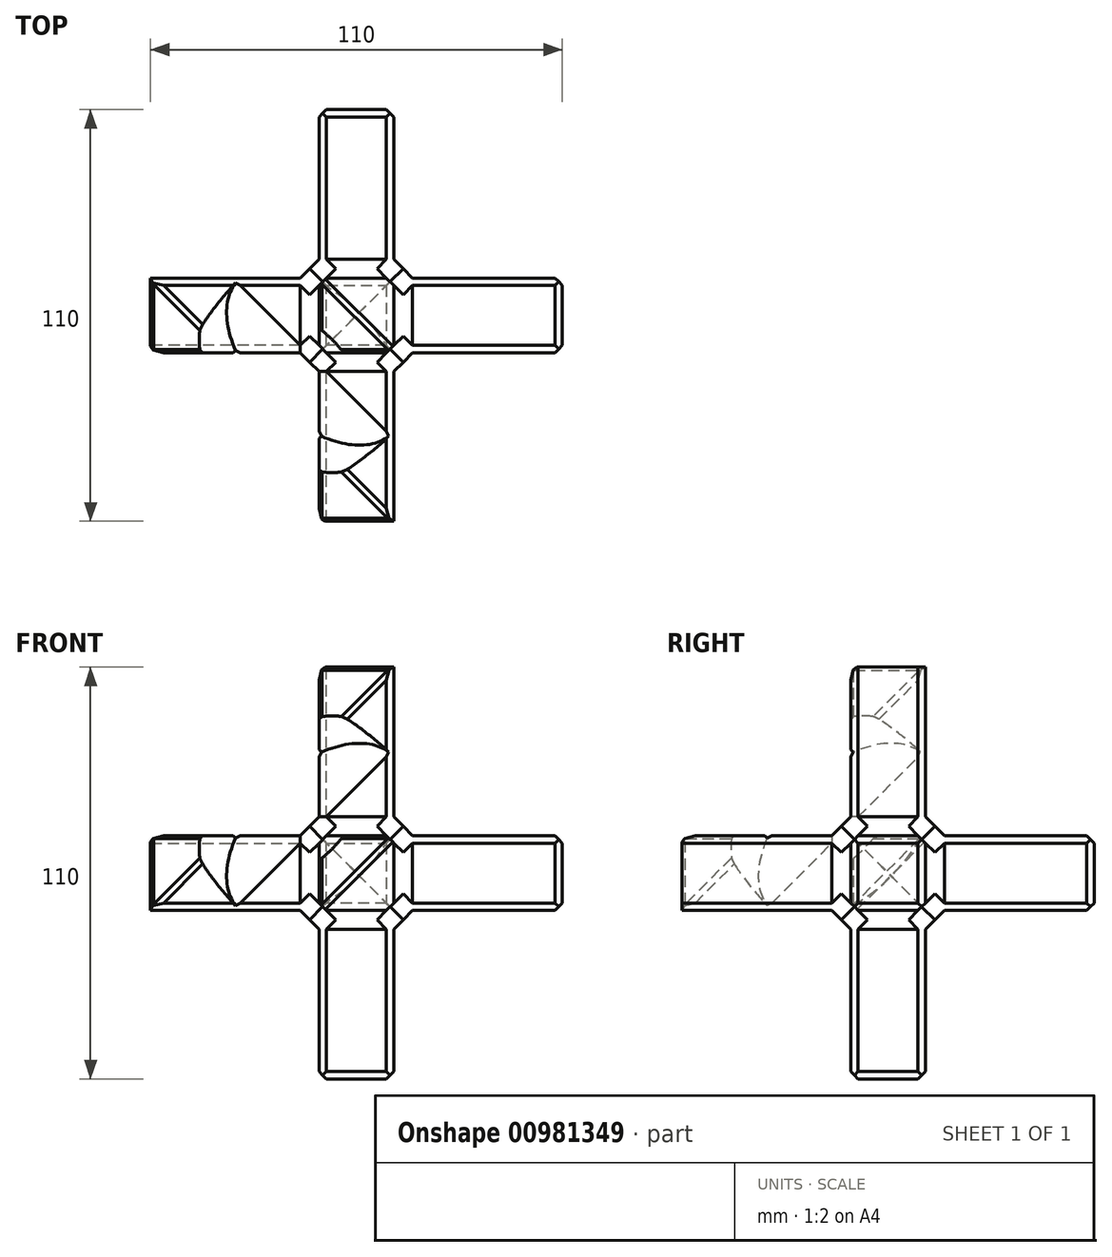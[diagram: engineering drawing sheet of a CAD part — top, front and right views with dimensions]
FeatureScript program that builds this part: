
annotation { "Feature Type Name" : "Feature", "Feature Type Description" : "" }
export const myFeature = defineFeature(function(context is Context, id is Id, definition is map)
    precondition{}
    {
        {
            assignVariable(context, id + "F0", {"name" : "longueur", "anyValue" : 110});
        }
        {
            assignVariable(context, id + "F1", {"name" : "HautBougie", "anyValue" : 23});
        }
        {
            var Q0;
            Q0=qCreatedBy(makeId("Top.planeOp"),FACE);
            var sketch = newSketch(context, id + "F2", { "sketchPlane" : qUnion([Q0])});
            skLineSegment(sketch, "E0.bottom", {"start": v(10, 10) * mm, "end": v(-10, 10) * mm});
            skLineSegment(sketch, "E0.top", {"start": v(10, -10) * mm, "end": v(-10, -10) * mm});
            skLineSegment(sketch, "E0.left", {"start": v(10, 10) * mm, "end": v(10, -10) * mm});
            skLineSegment(sketch, "E0.right", {"start": v(-10, 10) * mm, "end": v(-10, -10) * mm});
            skPoint(sketch, "E0.middle", {"position": v(0, 0) * mm});
            skSolve(sketch);
        }
        {
            var Q0;
            Q0 = qSketchRegion(id + "F2", true);
            extrude(context, id + "F3", {"entities" : qUnion([Q0]), "endBound" : BoundingType.SYMMETRIC, "depth" : (getVariable(context, 'longueur')) * mm, "offsetDistance" : 25 * mm});
        }
        {
            var Q0;
            Q0=qCreatedBy(makeId("Right.planeOp"),FACE);
            var sketch = newSketch(context, id + "F4", { "sketchPlane" : qUnion([Q0])});
            skLineSegment(sketch, "E1.bottom", {"start": v(-10, 10) * mm, "end": v(10, 10) * mm});
            skLineSegment(sketch, "E1.top", {"start": v(-10, -10) * mm, "end": v(10, -10) * mm});
            skLineSegment(sketch, "E1.left", {"start": v(-10, 10) * mm, "end": v(-10, -10) * mm});
            skLineSegment(sketch, "E1.right", {"start": v(10, 10) * mm, "end": v(10, -10) * mm});
            skPoint(sketch, "E1.middle", {"position": v(0, 0) * mm});
            skSolve(sketch);
        }
        {
            var Q0;
            Q0 = qSketchRegion(id + "F4", true);
            extrude(context, id + "F5", {"entities" : qUnion([Q0]), "operationType" : NewBodyOperationType.ADD, "endBound" : BoundingType.SYMMETRIC, "depth" : (getVariable(context, 'longueur')) * mm, "offsetDistance" : 25 * mm});
        }
        {
            var Q0;
            Q0=qCreatedBy(makeId("Front.planeOp"),FACE);
            var sketch = newSketch(context, id + "F6", { "sketchPlane" : qUnion([Q0])});
            skLineSegment(sketch, "E2.bottom", {"start": v(10, 10) * mm, "end": v(-10, 10) * mm});
            skLineSegment(sketch, "E2.top", {"start": v(10, -10) * mm, "end": v(-10, -10) * mm});
            skLineSegment(sketch, "E2.left", {"start": v(10, 10) * mm, "end": v(10, -10) * mm});
            skLineSegment(sketch, "E2.right", {"start": v(-10, 10) * mm, "end": v(-10, -10) * mm});
            skPoint(sketch, "E2.middle", {"position": v(0, 0) * mm});
            skSolve(sketch);
        }
        {
            var Q0;
            Q0 = qSketchRegion(id + "F6", true);
            extrude(context, id + "F7", {"entities" : qUnion([Q0]), "operationType" : NewBodyOperationType.ADD, "endBound" : BoundingType.SYMMETRIC, "depth" : (getVariable(context, 'longueur')) * mm, "offsetDistance" : 25 * mm});
        }
        {
            var Q0;
            Q0=makeQuery(id+"F7.opExtrude","CAP_VERTEX",VERTEX,{"disambiguationData":[OSD([sQuery(id+"F6.wireOp",EDGE,"E2.bottom"),sQuery(id+"F6.wireOp",EDGE,"E2.right")])],"isStart":false});
            var Q1;
            Q1=makeQuery(id+"F5.opExtrude","CAP_VERTEX",VERTEX,{"disambiguationData":[OSD([sQuery(id+"F4.wireOp",EDGE,"E1.bottom"),sQuery(id+"F4.wireOp",EDGE,"E1.left")])],"isStart":true});
            var Q2;
            Q2=makeQuery(id+"F3.opExtrude","CAP_VERTEX",VERTEX,{"disambiguationData":[OSD([sQuery(id+"F2.wireOp",EDGE,"E0.top"),sQuery(id+"F2.wireOp",EDGE,"E0.right")])],"isStart":false});
            cPlane(context, id + "F8", {"entities" : qUnion([Q0, Q1, Q2]), "cplaneType" : CPlaneType.THREE_POINT, "offset" : 25 * mm, "width" : 150 * mm, "height" : 150 * mm});
        }
        {
            var Q0;
            Q0=qCreatedBy(id+"F8.planeOp",FACE);
            var sketch = newSketch(context, id + "F9", { "sketchPlane" : qUnion([Q0])});
            skLineSegment(sketch, "E3.bottom", {"start": v(-58.75, 91.47) * mm, "end": v(80.41, 91.47) * mm});
            skLineSegment(sketch, "E3.top", {"start": v(-58.75, -91.47) * mm, "end": v(80.41, -91.47) * mm});
            skLineSegment(sketch, "E3.left", {"start": v(-58.75, 91.47) * mm, "end": v(-58.75, -91.47) * mm});
            skLineSegment(sketch, "E3.right", {"start": v(80.41, 91.47) * mm, "end": v(80.41, -91.47) * mm});
            skPoint(sketch, "E3.middle", {"position": v(10.83, 0) * mm});
            skSolve(sketch);
        }
        {
            var Q0;
            Q0 = qSketchRegion(id + "F9", true);
            var Q1;
            Q1=makeQuery(id+"F5.opExtrude","CAP_VERTEX",VERTEX,{"disambiguationData":[OSD([sQuery(id+"F4.wireOp",EDGE,"E1.top"),sQuery(id+"F4.wireOp",EDGE,"E1.left")])],"isStart":true});
            extrude(context, id + "F10", {"entities" : qUnion([Q0]), "operationType" : NewBodyOperationType.REMOVE, "endBound" : BoundingType.UP_TO_VERTEX, "oppositeDirection" : true, "depth" : 10 * mm, "endBoundEntityVertex" : qUnion([Q1]), "offsetDistance" : 25 * mm});
        }
        {
            var Q0;
            Q0=makeQuery(id+"F3.opExtrude","CAP_FACE",FACE,{"disambiguationData":[OSD([sQuery(id+"F2.wireOp",EDGE,"E0.bottom"),sQuery(id+"F2.wireOp",EDGE,"E0.top"),sQuery(id+"F2.wireOp",EDGE,"E0.left"),sQuery(id+"F2.wireOp",EDGE,"E0.right")])],"isStart":true});
            var Q1;
            Q1=makeQuery(id+"F7.opExtrude","CAP_FACE",FACE,{"disambiguationData":[OSD([sQuery(id+"F6.wireOp",EDGE,"E2.bottom"),sQuery(id+"F6.wireOp",EDGE,"E2.top"),sQuery(id+"F6.wireOp",EDGE,"E2.left"),sQuery(id+"F6.wireOp",EDGE,"E2.right")])],"isStart":true});
            var Q2;
            Q2=makeQuery(id+"F5.opExtrude","CAP_FACE",FACE,{"disambiguationData":[OSD([sQuery(id+"F4.wireOp",EDGE,"E1.bottom"),sQuery(id+"F4.wireOp",EDGE,"E1.top"),sQuery(id+"F4.wireOp",EDGE,"E1.left"),sQuery(id+"F4.wireOp",EDGE,"E1.right")])],"isStart":false});
            var Q3;
            {var subQ3=sQuery(id+"F4.wireOp",EDGE,"E1.bottom");Q3=makeQuery(id+"F10.boolean.opBoolean","COPY",FACE,{"disambiguationData":[TD([makeQuery(id+"F5.opExtrude","SWEPT_FACE",FACE,{"disambiguationData":[OSD([subQ3])]})])],"derivedFrom":makeQuery(id+"F10.opExtrude","CAP_FACE",FACE,{"disambiguationData":[OSD([sQuery(id+"F9.wireOp",EDGE,"E3.bottom"),sQuery(id+"F9.wireOp",EDGE,"E3.top"),sQuery(id+"F9.wireOp",EDGE,"E3.left"),sQuery(id+"F9.wireOp",EDGE,"E3.right")])],"isStart":false})});}
            var Q4;
            {var subQ3=sQuery(id+"F6.wireOp",EDGE,"E2.bottom");Q4=makeQuery(id+"F10.boolean.opBoolean","COPY",FACE,{"disambiguationData":[TD([makeQuery(id+"F7.opExtrude","SWEPT_FACE",FACE,{"disambiguationData":[OSD([subQ3])]})])],"derivedFrom":makeQuery(id+"F10.opExtrude","CAP_FACE",FACE,{"disambiguationData":[OSD([sQuery(id+"F9.wireOp",EDGE,"E3.bottom"),sQuery(id+"F9.wireOp",EDGE,"E3.top"),sQuery(id+"F9.wireOp",EDGE,"E3.left"),sQuery(id+"F9.wireOp",EDGE,"E3.right")])],"isStart":false})});}
            var Q5;
            {var subQ0=sQuery(id+"F2.wireOp",EDGE,"E0.left");Q5=makeQuery(id+"F10.boolean.opBoolean","COPY",FACE,{"disambiguationData":[TD([makeQuery(id+"F3.opExtrude","SWEPT_FACE",FACE,{"disambiguationData":[OSD([subQ0])]})])],"derivedFrom":makeQuery(id+"F10.opExtrude","CAP_FACE",FACE,{"disambiguationData":[OSD([sQuery(id+"F9.wireOp",EDGE,"E3.bottom"),sQuery(id+"F9.wireOp",EDGE,"E3.top"),sQuery(id+"F9.wireOp",EDGE,"E3.left"),sQuery(id+"F9.wireOp",EDGE,"E3.right")])],"isStart":false})});}
            chamfer(context, id + "F11", {"entities" : qUnion([Q0, Q1, Q2, Q3, Q4, Q5]), "width" : 2 * mm, "tangentPropagation" : true});
        }
        {
            var Q0;
            {var subQ0=sQuery(id+"F2.wireOp",EDGE,"E0.left");var subQ1=sQuery(id+"F2.wireOp",EDGE,"E0.top");Q0=makeQuery(id+"F5.boolean.opBoolean","SPLIT",EDGE,{"disambiguationData":[TD([makeQuery(id+"F5.opExtrude","SWEPT_FACE",FACE,{"disambiguationData":[OSD([sQuery(id+"F4.wireOp",EDGE,"E1.bottom")])]})])],"derivedFrom":makeQuery(id+"F3.opExtrude","SWEPT_EDGE",EDGE,{"disambiguationData":[OSD([subQ1,subQ0])]})});}
            var Q1;
            {var subQ0=sQuery(id+"F2.wireOp",EDGE,"E0.left");var subQ1=sQuery(id+"F2.wireOp",EDGE,"E0.bottom");Q1=makeQuery(id+"F5.boolean.opBoolean","SPLIT",EDGE,{"disambiguationData":[TD([makeQuery(id+"F5.opExtrude","SWEPT_FACE",FACE,{"disambiguationData":[OSD([sQuery(id+"F4.wireOp",EDGE,"E1.bottom")])]})])],"derivedFrom":makeQuery(id+"F3.opExtrude","SWEPT_EDGE",EDGE,{"disambiguationData":[OSD([subQ1,subQ0])]})});}
            var Q2;
            {var subQ0=sQuery(id+"F2.wireOp",EDGE,"E0.right");var subQ1=sQuery(id+"F2.wireOp",EDGE,"E0.bottom");Q2=makeQuery(id+"F5.boolean.opBoolean","SPLIT",EDGE,{"disambiguationData":[TD([makeQuery(id+"F5.opExtrude","SWEPT_FACE",FACE,{"disambiguationData":[OSD([sQuery(id+"F4.wireOp",EDGE,"E1.bottom")])]})])],"derivedFrom":makeQuery(id+"F3.opExtrude","SWEPT_EDGE",EDGE,{"disambiguationData":[OSD([subQ1,subQ0])]})});}
            var Q3;
            {var subQ0=sQuery(id+"F2.wireOp",EDGE,"E0.left");var subQ1=sQuery(id+"F2.wireOp",EDGE,"E0.top");Q3=makeQuery(id+"F5.boolean.opBoolean","SPLIT",EDGE,{"disambiguationData":[TD([makeQuery(id+"F5.opExtrude","SWEPT_FACE",FACE,{"disambiguationData":[OSD([sQuery(id+"F4.wireOp",EDGE,"E1.top")])]})])],"derivedFrom":makeQuery(id+"F3.opExtrude","SWEPT_EDGE",EDGE,{"disambiguationData":[OSD([subQ1,subQ0])]})});}
            var Q4;
            {var subQ0=sQuery(id+"F2.wireOp",EDGE,"E0.right");var subQ1=sQuery(id+"F2.wireOp",EDGE,"E0.top");Q4=makeQuery(id+"F5.boolean.opBoolean","SPLIT",EDGE,{"disambiguationData":[TD([makeQuery(id+"F5.opExtrude","SWEPT_FACE",FACE,{"disambiguationData":[OSD([sQuery(id+"F4.wireOp",EDGE,"E1.top")])]})])],"derivedFrom":makeQuery(id+"F3.opExtrude","SWEPT_EDGE",EDGE,{"disambiguationData":[OSD([subQ1,subQ0])]})});}
            var Q5;
            {var subQ0=sQuery(id+"F2.wireOp",EDGE,"E0.right");var subQ1=sQuery(id+"F2.wireOp",EDGE,"E0.bottom");Q5=makeQuery(id+"F5.boolean.opBoolean","SPLIT",EDGE,{"disambiguationData":[TD([makeQuery(id+"F5.opExtrude","SWEPT_FACE",FACE,{"disambiguationData":[OSD([sQuery(id+"F4.wireOp",EDGE,"E1.top")])]})])],"derivedFrom":makeQuery(id+"F3.opExtrude","SWEPT_EDGE",EDGE,{"disambiguationData":[OSD([subQ1,subQ0])]})});}
            var Q6;
            {var subQ0=sQuery(id+"F2.wireOp",EDGE,"E0.left");var subQ1=sQuery(id+"F2.wireOp",EDGE,"E0.bottom");Q6=makeQuery(id+"F5.boolean.opBoolean","SPLIT",EDGE,{"disambiguationData":[TD([makeQuery(id+"F5.opExtrude","SWEPT_FACE",FACE,{"disambiguationData":[OSD([sQuery(id+"F4.wireOp",EDGE,"E1.top")])]})])],"derivedFrom":makeQuery(id+"F3.opExtrude","SWEPT_EDGE",EDGE,{"disambiguationData":[OSD([subQ1,subQ0])]})});}
            var Q7;
            {var subQ0=sQuery(id+"F2.wireOp",EDGE,"E0.right");var subQ1=sQuery(id+"F2.wireOp",EDGE,"E0.top");Q7=makeQuery(id+"F5.boolean.opBoolean","SPLIT",EDGE,{"disambiguationData":[TD([makeQuery(id+"F5.opExtrude","SWEPT_FACE",FACE,{"disambiguationData":[OSD([sQuery(id+"F4.wireOp",EDGE,"E1.bottom")])]})])],"derivedFrom":makeQuery(id+"F3.opExtrude","SWEPT_EDGE",EDGE,{"disambiguationData":[OSD([subQ1,subQ0])]})});}
            chamfer(context, id + "F12", {"entities" : qUnion([Q0, Q1, Q2, Q3, Q4, Q5, Q6, Q7]), "width" : 2 * mm, "tangentPropagation" : true});
        }
        {
            var Q0;
            {var subQ0=sQuery(id+"F4.wireOp",EDGE,"E1.top");var subQ1=sQuery(id+"F4.wireOp",EDGE,"E1.left");Q0=makeQuery(id+"F5.boolean.opBoolean","SPLIT",EDGE,{"disambiguationData":[TD([makeQuery(id+"F3.opExtrude","SWEPT_FACE",FACE,{"disambiguationData":[OSD([sQuery(id+"F2.wireOp",EDGE,"E0.left")])]})])],"derivedFrom":makeQuery(id+"F5.opExtrude","SWEPT_EDGE",EDGE,{"disambiguationData":[OSD([subQ0,subQ1])]})});}
            var Q1;
            {var subQ0=sQuery(id+"F4.wireOp",EDGE,"E1.top");var subQ1=sQuery(id+"F4.wireOp",EDGE,"E1.right");Q1=makeQuery(id+"F5.boolean.opBoolean","SPLIT",EDGE,{"disambiguationData":[TD([makeQuery(id+"F3.opExtrude","SWEPT_FACE",FACE,{"disambiguationData":[OSD([sQuery(id+"F2.wireOp",EDGE,"E0.left")])]})])],"derivedFrom":makeQuery(id+"F5.opExtrude","SWEPT_EDGE",EDGE,{"disambiguationData":[OSD([subQ0,subQ1])]})});}
            var Q2;
            {var subQ0=sQuery(id+"F4.wireOp",EDGE,"E1.top");var subQ1=sQuery(id+"F4.wireOp",EDGE,"E1.left");Q2=makeQuery(id+"F5.boolean.opBoolean","SPLIT",EDGE,{"disambiguationData":[TD([makeQuery(id+"F3.opExtrude","SWEPT_FACE",FACE,{"disambiguationData":[OSD([sQuery(id+"F2.wireOp",EDGE,"E0.right")])]})])],"derivedFrom":makeQuery(id+"F5.opExtrude","SWEPT_EDGE",EDGE,{"disambiguationData":[OSD([subQ0,subQ1])]})});}
            var Q3;
            {var subQ0=sQuery(id+"F4.wireOp",EDGE,"E1.top");var subQ1=sQuery(id+"F4.wireOp",EDGE,"E1.right");Q3=makeQuery(id+"F5.boolean.opBoolean","SPLIT",EDGE,{"disambiguationData":[TD([makeQuery(id+"F3.opExtrude","SWEPT_FACE",FACE,{"disambiguationData":[OSD([sQuery(id+"F2.wireOp",EDGE,"E0.right")])]})])],"derivedFrom":makeQuery(id+"F5.opExtrude","SWEPT_EDGE",EDGE,{"disambiguationData":[OSD([subQ0,subQ1])]})});}
            var Q4;
            {var subQ0=sQuery(id+"F4.wireOp",EDGE,"E1.left");var subQ1=sQuery(id+"F4.wireOp",EDGE,"E1.bottom");Q4=makeQuery(id+"F5.boolean.opBoolean","SPLIT",EDGE,{"disambiguationData":[TD([makeQuery(id+"F3.opExtrude","SWEPT_FACE",FACE,{"disambiguationData":[OSD([sQuery(id+"F2.wireOp",EDGE,"E0.left")])]})])],"derivedFrom":makeQuery(id+"F5.opExtrude","SWEPT_EDGE",EDGE,{"disambiguationData":[OSD([subQ1,subQ0])]})});}
            var Q5;
            {var subQ0=sQuery(id+"F4.wireOp",EDGE,"E1.bottom");var subQ1=sQuery(id+"F4.wireOp",EDGE,"E1.right");Q5=makeQuery(id+"F5.boolean.opBoolean","SPLIT",EDGE,{"disambiguationData":[TD([makeQuery(id+"F3.opExtrude","SWEPT_FACE",FACE,{"disambiguationData":[OSD([sQuery(id+"F2.wireOp",EDGE,"E0.left")])]})])],"derivedFrom":makeQuery(id+"F5.opExtrude","SWEPT_EDGE",EDGE,{"disambiguationData":[OSD([subQ0,subQ1])]})});}
            var Q6;
            {var subQ0=sQuery(id+"F4.wireOp",EDGE,"E1.right");var subQ1=sQuery(id+"F4.wireOp",EDGE,"E1.bottom");Q6=makeQuery(id+"F5.boolean.opBoolean","SPLIT",EDGE,{"disambiguationData":[TD([makeQuery(id+"F3.opExtrude","SWEPT_FACE",FACE,{"disambiguationData":[OSD([sQuery(id+"F2.wireOp",EDGE,"E0.right")])]})])],"derivedFrom":makeQuery(id+"F5.opExtrude","SWEPT_EDGE",EDGE,{"disambiguationData":[OSD([subQ1,subQ0])]})});}
            var Q7;
            {var subQ0=sQuery(id+"F4.wireOp",EDGE,"E1.left");var subQ1=sQuery(id+"F4.wireOp",EDGE,"E1.bottom");Q7=makeQuery(id+"F5.boolean.opBoolean","SPLIT",EDGE,{"disambiguationData":[TD([makeQuery(id+"F3.opExtrude","SWEPT_FACE",FACE,{"disambiguationData":[OSD([sQuery(id+"F2.wireOp",EDGE,"E0.right")])]})])],"derivedFrom":makeQuery(id+"F5.opExtrude","SWEPT_EDGE",EDGE,{"disambiguationData":[OSD([subQ1,subQ0])]})});}
            chamfer(context, id + "F13", {"entities" : qUnion([Q0, Q1, Q2, Q3, Q4, Q5, Q6, Q7]), "width" : 2 * mm, "tangentPropagation" : true});
        }
        {
            var Q0;
            {var subQ0=sQuery(id+"F6.wireOp",EDGE,"E2.left");var subQ1=sQuery(id+"F6.wireOp",EDGE,"E2.top");Q0=makeQuery(id+"F7.boolean.opBoolean","SPLIT",EDGE,{"disambiguationData":[TD([makeQuery(id+"F3.opExtrude","SWEPT_FACE",FACE,{"disambiguationData":[OSD([sQuery(id+"F2.wireOp",EDGE,"E0.bottom")])]})])],"derivedFrom":makeQuery(id+"F7.opExtrude","SWEPT_EDGE",EDGE,{"disambiguationData":[OSD([subQ1,subQ0])]})});}
            var Q1;
            {var subQ0=sQuery(id+"F6.wireOp",EDGE,"E2.bottom");var subQ1=sQuery(id+"F6.wireOp",EDGE,"E2.left");Q1=makeQuery(id+"F7.boolean.opBoolean","SPLIT",EDGE,{"disambiguationData":[TD([makeQuery(id+"F3.opExtrude","SWEPT_FACE",FACE,{"disambiguationData":[OSD([sQuery(id+"F2.wireOp",EDGE,"E0.bottom")])]})])],"derivedFrom":makeQuery(id+"F7.opExtrude","SWEPT_EDGE",EDGE,{"disambiguationData":[OSD([subQ0,subQ1])]})});}
            var Q2;
            {var subQ0=sQuery(id+"F6.wireOp",EDGE,"E2.bottom");var subQ1=sQuery(id+"F6.wireOp",EDGE,"E2.left");Q2=makeQuery(id+"F7.boolean.opBoolean","SPLIT",EDGE,{"disambiguationData":[TD([makeQuery(id+"F3.opExtrude","SWEPT_FACE",FACE,{"disambiguationData":[OSD([sQuery(id+"F2.wireOp",EDGE,"E0.top")])]})])],"derivedFrom":makeQuery(id+"F7.opExtrude","SWEPT_EDGE",EDGE,{"disambiguationData":[OSD([subQ0,subQ1])]})});}
            var Q3;
            {var subQ0=sQuery(id+"F6.wireOp",EDGE,"E2.bottom");var subQ1=sQuery(id+"F6.wireOp",EDGE,"E2.right");Q3=makeQuery(id+"F7.boolean.opBoolean","SPLIT",EDGE,{"disambiguationData":[TD([makeQuery(id+"F3.opExtrude","SWEPT_FACE",FACE,{"disambiguationData":[OSD([sQuery(id+"F2.wireOp",EDGE,"E0.bottom")])]})])],"derivedFrom":makeQuery(id+"F7.opExtrude","SWEPT_EDGE",EDGE,{"disambiguationData":[OSD([subQ0,subQ1])]})});}
            var Q4;
            {var subQ0=sQuery(id+"F6.wireOp",EDGE,"E2.right");var subQ1=sQuery(id+"F6.wireOp",EDGE,"E2.top");Q4=makeQuery(id+"F7.boolean.opBoolean","SPLIT",EDGE,{"disambiguationData":[TD([makeQuery(id+"F3.opExtrude","SWEPT_FACE",FACE,{"disambiguationData":[OSD([sQuery(id+"F2.wireOp",EDGE,"E0.bottom")])]})])],"derivedFrom":makeQuery(id+"F7.opExtrude","SWEPT_EDGE",EDGE,{"disambiguationData":[OSD([subQ1,subQ0])]})});}
            var Q5;
            {var subQ0=sQuery(id+"F6.wireOp",EDGE,"E2.right");var subQ1=sQuery(id+"F6.wireOp",EDGE,"E2.top");Q5=makeQuery(id+"F7.boolean.opBoolean","SPLIT",EDGE,{"disambiguationData":[TD([makeQuery(id+"F3.opExtrude","SWEPT_FACE",FACE,{"disambiguationData":[OSD([sQuery(id+"F2.wireOp",EDGE,"E0.top")])]})])],"derivedFrom":makeQuery(id+"F7.opExtrude","SWEPT_EDGE",EDGE,{"disambiguationData":[OSD([subQ1,subQ0])]})});}
            var Q6;
            {var subQ0=sQuery(id+"F6.wireOp",EDGE,"E2.left");var subQ1=sQuery(id+"F6.wireOp",EDGE,"E2.top");Q6=makeQuery(id+"F7.boolean.opBoolean","SPLIT",EDGE,{"disambiguationData":[TD([makeQuery(id+"F3.opExtrude","SWEPT_FACE",FACE,{"disambiguationData":[OSD([sQuery(id+"F2.wireOp",EDGE,"E0.top")])]})])],"derivedFrom":makeQuery(id+"F7.opExtrude","SWEPT_EDGE",EDGE,{"disambiguationData":[OSD([subQ1,subQ0])]})});}
            var Q7;
            {var subQ0=sQuery(id+"F6.wireOp",EDGE,"E2.bottom");var subQ1=sQuery(id+"F6.wireOp",EDGE,"E2.right");Q7=makeQuery(id+"F7.boolean.opBoolean","SPLIT",EDGE,{"disambiguationData":[TD([makeQuery(id+"F3.opExtrude","SWEPT_FACE",FACE,{"disambiguationData":[OSD([sQuery(id+"F2.wireOp",EDGE,"E0.top")])]})])],"derivedFrom":makeQuery(id+"F7.opExtrude","SWEPT_EDGE",EDGE,{"disambiguationData":[OSD([subQ0,subQ1])]})});}
            chamfer(context, id + "F14", {"entities" : qUnion([Q0, Q1, Q2, Q3, Q4, Q5, Q6, Q7]), "width" : 2 * mm, "tangentPropagation" : true});
        }
        {
            var Q0;
            Q0=makeQuery(id+"F7.boolean.opBoolean","INTERSECT",EDGE,{"derivedFrom":[makeQuery(id+"F5.boolean.opBoolean","MERGE",FACE,{"derivedFrom":[makeQuery(id+"F3.opExtrude","SWEPT_FACE",FACE,{"disambiguationData":[OSD([sQuery(id+"F2.wireOp",EDGE,"E0.bottom")])]}),makeQuery(id+"F5.opExtrude","SWEPT_FACE",FACE,{"disambiguationData":[OSD([sQuery(id+"F4.wireOp",EDGE,"E1.right")])]})]}),makeQuery(id+"F7.opExtrude","SWEPT_FACE",FACE,{"disambiguationData":[OSD([sQuery(id+"F6.wireOp",EDGE,"E2.top")])]})]});
            var Q1;
            Q1=makeQuery(id+"F7.boolean.opBoolean","INTERSECT",EDGE,{"derivedFrom":[makeQuery(id+"F5.boolean.opBoolean","MERGE",FACE,{"derivedFrom":[makeQuery(id+"F3.opExtrude","SWEPT_FACE",FACE,{"disambiguationData":[OSD([sQuery(id+"F2.wireOp",EDGE,"E0.bottom")])]}),makeQuery(id+"F5.opExtrude","SWEPT_FACE",FACE,{"disambiguationData":[OSD([sQuery(id+"F4.wireOp",EDGE,"E1.right")])]})]}),makeQuery(id+"F7.opExtrude","SWEPT_FACE",FACE,{"disambiguationData":[OSD([sQuery(id+"F6.wireOp",EDGE,"E2.left")])]})]});
            var Q2;
            Q2=makeQuery(id+"F7.boolean.opBoolean","INTERSECT",EDGE,{"derivedFrom":[makeQuery(id+"F5.boolean.opBoolean","MERGE",FACE,{"derivedFrom":[makeQuery(id+"F3.opExtrude","SWEPT_FACE",FACE,{"disambiguationData":[OSD([sQuery(id+"F2.wireOp",EDGE,"E0.bottom")])]}),makeQuery(id+"F5.opExtrude","SWEPT_FACE",FACE,{"disambiguationData":[OSD([sQuery(id+"F4.wireOp",EDGE,"E1.right")])]})]}),makeQuery(id+"F7.opExtrude","SWEPT_FACE",FACE,{"disambiguationData":[OSD([sQuery(id+"F6.wireOp",EDGE,"E2.bottom")])]})]});
            var Q3;
            Q3=makeQuery(id+"F7.boolean.opBoolean","INTERSECT",EDGE,{"derivedFrom":[makeQuery(id+"F5.boolean.opBoolean","MERGE",FACE,{"derivedFrom":[makeQuery(id+"F3.opExtrude","SWEPT_FACE",FACE,{"disambiguationData":[OSD([sQuery(id+"F2.wireOp",EDGE,"E0.bottom")])]}),makeQuery(id+"F5.opExtrude","SWEPT_FACE",FACE,{"disambiguationData":[OSD([sQuery(id+"F4.wireOp",EDGE,"E1.right")])]})]}),makeQuery(id+"F7.opExtrude","SWEPT_FACE",FACE,{"disambiguationData":[OSD([sQuery(id+"F6.wireOp",EDGE,"E2.right")])]})]});
            var Q4;
            Q4=makeQuery(id+"F7.boolean.opBoolean","INTERSECT",EDGE,{"derivedFrom":[makeQuery(id+"F5.boolean.opBoolean","MERGE",FACE,{"derivedFrom":[makeQuery(id+"F3.opExtrude","SWEPT_FACE",FACE,{"disambiguationData":[OSD([sQuery(id+"F2.wireOp",EDGE,"E0.top")])]}),makeQuery(id+"F5.opExtrude","SWEPT_FACE",FACE,{"disambiguationData":[OSD([sQuery(id+"F4.wireOp",EDGE,"E1.left")])]})]}),makeQuery(id+"F7.opExtrude","SWEPT_FACE",FACE,{"disambiguationData":[OSD([sQuery(id+"F6.wireOp",EDGE,"E2.top")])]})]});
            var Q5;
            Q5=makeQuery(id+"F5.boolean.opBoolean","INTERSECT",EDGE,{"derivedFrom":[makeQuery(id+"F3.opExtrude","SWEPT_FACE",FACE,{"disambiguationData":[OSD([sQuery(id+"F2.wireOp",EDGE,"E0.left")])]}),makeQuery(id+"F5.opExtrude","SWEPT_FACE",FACE,{"disambiguationData":[OSD([sQuery(id+"F4.wireOp",EDGE,"E1.top")])]})]});
            var Q6;
            Q6=makeQuery(id+"F5.boolean.opBoolean","INTERSECT",EDGE,{"derivedFrom":[makeQuery(id+"F3.opExtrude","SWEPT_FACE",FACE,{"disambiguationData":[OSD([sQuery(id+"F2.wireOp",EDGE,"E0.left")])]}),makeQuery(id+"F5.opExtrude","SWEPT_FACE",FACE,{"disambiguationData":[OSD([sQuery(id+"F4.wireOp",EDGE,"E1.bottom")])]})]});
            var Q7;
            Q7=makeQuery(id+"F5.boolean.opBoolean","INTERSECT",EDGE,{"derivedFrom":[makeQuery(id+"F3.opExtrude","SWEPT_FACE",FACE,{"disambiguationData":[OSD([sQuery(id+"F2.wireOp",EDGE,"E0.right")])]}),makeQuery(id+"F5.opExtrude","SWEPT_FACE",FACE,{"disambiguationData":[OSD([sQuery(id+"F4.wireOp",EDGE,"E1.bottom")])]})]});
            var Q8;
            Q8=makeQuery(id+"F7.boolean.opBoolean","INTERSECT",EDGE,{"derivedFrom":[makeQuery(id+"F5.boolean.opBoolean","MERGE",FACE,{"derivedFrom":[makeQuery(id+"F3.opExtrude","SWEPT_FACE",FACE,{"disambiguationData":[OSD([sQuery(id+"F2.wireOp",EDGE,"E0.top")])]}),makeQuery(id+"F5.opExtrude","SWEPT_FACE",FACE,{"disambiguationData":[OSD([sQuery(id+"F4.wireOp",EDGE,"E1.left")])]})]}),makeQuery(id+"F7.opExtrude","SWEPT_FACE",FACE,{"disambiguationData":[OSD([sQuery(id+"F6.wireOp",EDGE,"E2.bottom")])]})]});
            var Q9;
            Q9=makeQuery(id+"F7.boolean.opBoolean","INTERSECT",EDGE,{"derivedFrom":[makeQuery(id+"F5.boolean.opBoolean","MERGE",FACE,{"derivedFrom":[makeQuery(id+"F3.opExtrude","SWEPT_FACE",FACE,{"disambiguationData":[OSD([sQuery(id+"F2.wireOp",EDGE,"E0.top")])]}),makeQuery(id+"F5.opExtrude","SWEPT_FACE",FACE,{"disambiguationData":[OSD([sQuery(id+"F4.wireOp",EDGE,"E1.left")])]})]}),makeQuery(id+"F7.opExtrude","SWEPT_FACE",FACE,{"disambiguationData":[OSD([sQuery(id+"F6.wireOp",EDGE,"E2.right")])]})]});
            var Q10;
            Q10=makeQuery(id+"F5.boolean.opBoolean","INTERSECT",EDGE,{"derivedFrom":[makeQuery(id+"F3.opExtrude","SWEPT_FACE",FACE,{"disambiguationData":[OSD([sQuery(id+"F2.wireOp",EDGE,"E0.right")])]}),makeQuery(id+"F5.opExtrude","SWEPT_FACE",FACE,{"disambiguationData":[OSD([sQuery(id+"F4.wireOp",EDGE,"E1.top")])]})]});
            var Q11;
            Q11=makeQuery(id+"F7.boolean.opBoolean","INTERSECT",EDGE,{"derivedFrom":[makeQuery(id+"F5.boolean.opBoolean","MERGE",FACE,{"derivedFrom":[makeQuery(id+"F3.opExtrude","SWEPT_FACE",FACE,{"disambiguationData":[OSD([sQuery(id+"F2.wireOp",EDGE,"E0.top")])]}),makeQuery(id+"F5.opExtrude","SWEPT_FACE",FACE,{"disambiguationData":[OSD([sQuery(id+"F4.wireOp",EDGE,"E1.left")])]})]}),makeQuery(id+"F7.opExtrude","SWEPT_FACE",FACE,{"disambiguationData":[OSD([sQuery(id+"F6.wireOp",EDGE,"E2.left")])]})]});
            chamfer(context, id + "F15", {"entities" : qUnion([Q0, Q1, Q2, Q3, Q4, Q5, Q6, Q7, Q8, Q9, Q10, Q11]), "width" : 5 * mm, "tangentPropagation" : true});
        }
        {
            var Q0;
            Q0=qCreatedBy(id+"F8.planeOp",FACE);
            var sketch = newSketch(context, id + "F16", { "sketchPlane" : qUnion([Q0])});
            skCircle(sketch, "E4", {"center": v(0, 0) * mm, "radius": 0.03 * mm});
            skSolve(sketch);
        }
        {
            var Q0;
            Q0 = qSketchRegion(id + "F16", true);
            extrude(context, id + "F17", {"entities" : qUnion([Q0]), "operationType" : NewBodyOperationType.REMOVE, "endBound" : BoundingType.THROUGH_ALL, "oppositeDirection" : true, "depth" : 25 * mm, "offsetDistance" : 25 * mm});
        }
        {
            var Q0;
            Q0=qCreatedBy(id+"F8.planeOp",FACE);
            var sketch = newSketch(context, id + "F18", { "sketchPlane" : qUnion([Q0])});
            skCircle(sketch, "E5", {"center": v(0, 0) * mm, "radius": 29 * mm});
            skSolve(sketch);
        }
        {
            var Q0;
            Q0 = qSketchRegion(id + "F18", true);
            var Q1;
            {var subQ0=sQuery(id+"F2.wireOp",EDGE,"E0.right");var subQ1=sQuery(id+"F2.wireOp",EDGE,"E0.top");Q1=makeQuery(id+"F12.opChamfer","BLEND_FACE",FACE,{"disambiguationData":[OSD([subQ1,subQ0]),TDD([makeQuery(id+"F5.boolean.opBoolean","SPLIT",EDGE,{"disambiguationData":[TD([makeQuery(id+"F5.opExtrude","SWEPT_FACE",FACE,{"disambiguationData":[OSD([sQuery(id+"F4.wireOp",EDGE,"E1.bottom")])]})])],"derivedFrom":makeQuery(id+"F3.opExtrude","SWEPT_EDGE",EDGE,{"disambiguationData":[OSD([subQ1,subQ0])]})})])]});}
            var Q2;
            {var subQ0=sQuery(id+"F2.wireOp",EDGE,"E0.right");var subQ1=makeQuery(id+"F3.opExtrude","SWEPT_FACE",FACE,{"disambiguationData":[OSD([subQ0])]});var subQ3=makeQuery(id+"F5.opExtrude","SWEPT_FACE",FACE,{"disambiguationData":[OSD([sQuery(id+"F4.wireOp",EDGE,"E1.bottom")])]});var subQ4=sQuery(id+"F2.wireOp",EDGE,"E0.top");Q2=makeQuery(id+"F15.opChamfer","BLEND_VERTEX",VERTEX,{"blendedFrom":[makeQuery(id+"F5.boolean.opBoolean","INTERSECT",EDGE,{"derivedFrom":[subQ1,subQ3]}),makeQuery(id+"F5.boolean.opBoolean","SPLIT",FACE,{"disambiguationData":[TD([subQ3])],"derivedFrom":subQ1}),makeQuery(id+"F12.opChamfer","BLEND_FACE",FACE,{"disambiguationData":[OSD([subQ4,subQ0]),TDD([makeQuery(id+"F5.boolean.opBoolean","SPLIT",EDGE,{"disambiguationData":[TD([subQ3])],"derivedFrom":makeQuery(id+"F3.opExtrude","SWEPT_EDGE",EDGE,{"disambiguationData":[OSD([subQ4,subQ0])]})})])]})],"blendedInto":[makeQuery(id+"F5.boolean.opBoolean","SPLIT",FACE,{"disambiguationData":[TD([subQ3])],"derivedFrom":subQ1}),makeQuery(id+"F12.opChamfer","BLEND_FACE",FACE,{"disambiguationData":[OSD([subQ4,subQ0]),TDD([makeQuery(id+"F5.boolean.opBoolean","SPLIT",EDGE,{"disambiguationData":[TD([subQ3])],"derivedFrom":makeQuery(id+"F3.opExtrude","SWEPT_EDGE",EDGE,{"disambiguationData":[OSD([subQ4,subQ0])]})})])]})]});}
            extrude(context, id + "F19", {"entities" : qUnion([Q0, Q1]), "operationType" : NewBodyOperationType.REMOVE, "endBound" : BoundingType.UP_TO_VERTEX, "oppositeDirection" : true, "depth" : (getVariable(context, 'HautBougie')) * mm, "endBoundEntityVertex" : qUnion([Q2]), "offsetDistance" : 25 * mm});
        }
    });
